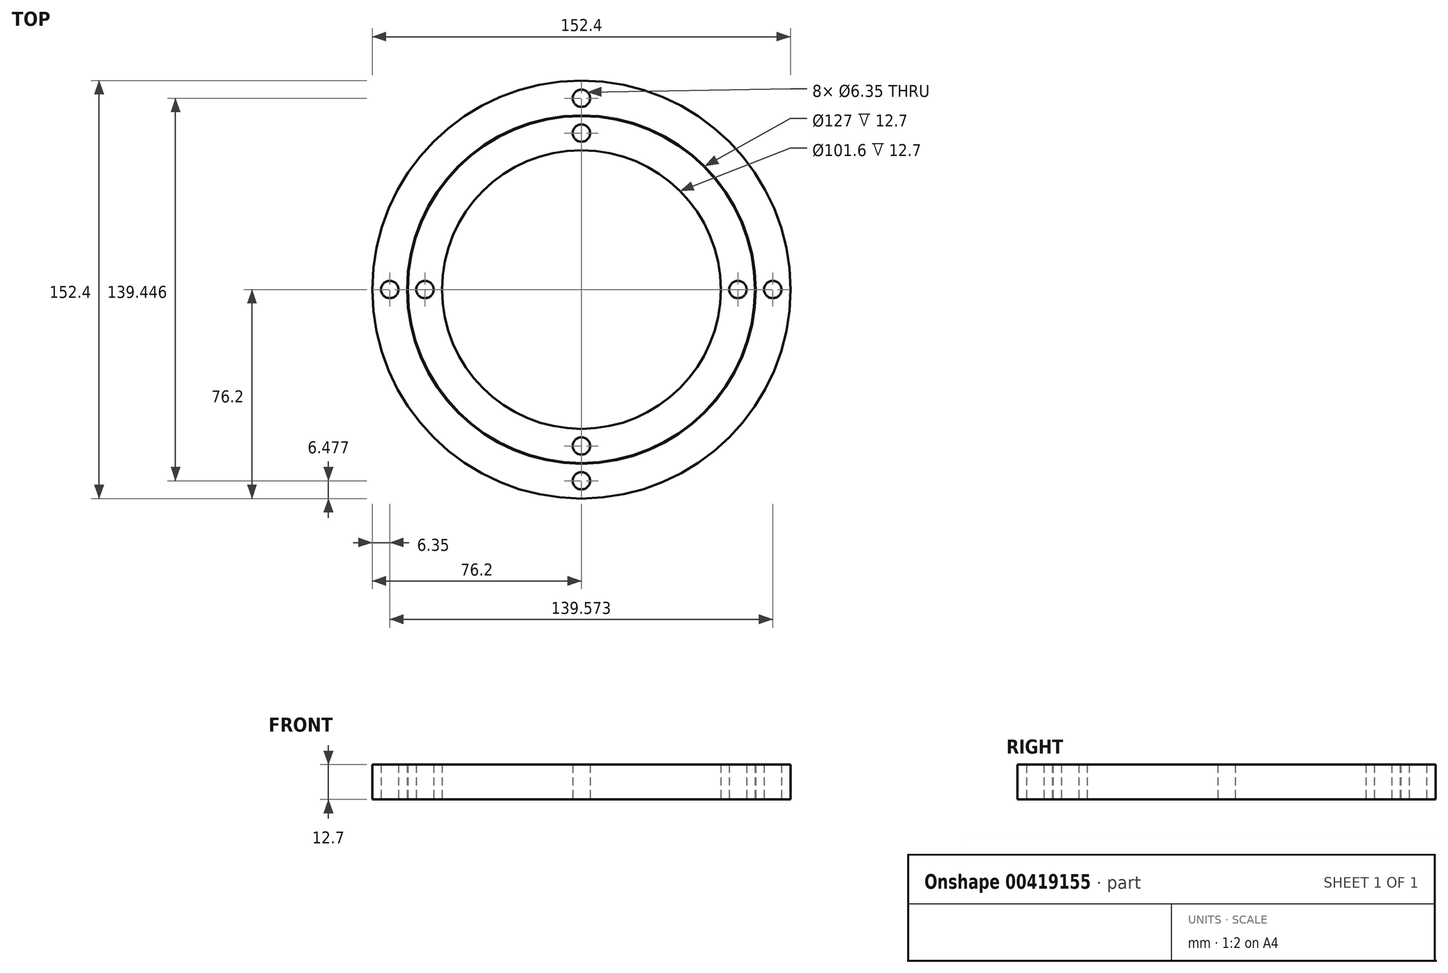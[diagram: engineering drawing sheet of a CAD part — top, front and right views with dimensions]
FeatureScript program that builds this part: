
annotation { "Feature Type Name" : "Feature", "Feature Type Description" : "" }
export const myFeature = defineFeature(function(context is Context, id is Id, definition is map)
    precondition{}
    {
        {
            var Q0;
            Q0=qCreatedBy(makeId("Top.planeOp"),FACE);
            var sketch = newSketch(context, id + "F0", { "sketchPlane" : qUnion([Q0])});
            skCircle(sketch, "E0", {"center": v(0, 0) * mm, "radius": 76.2 * mm});
            skCircle(sketch, "E1", {"center": v(0, 0) * mm, "radius": 63.5 * mm});
            skCircle(sketch, "E2", {"center": v(0, 0) * mm, "radius": 50.8 * mm});
            skCircle(sketch, "E3", {"center": v(0, 0) * mm, "radius": 63.25 * mm});
            skLineSegment(sketch, "E4", {"start": v(-76.2, 0) * mm, "end": v(-63.5, 0) * mm});
            skLineSegment(sketch, "E5", {"start": v(0, 76.2) * mm, "end": v(0, 63.25) * mm});
            skLineSegment(sketch, "E6", {"start": v(63.25, 0) * mm, "end": v(76.2, 0) * mm});
            skLineSegment(sketch, "E7", {"start": v(0, 50.8) * mm, "end": v(0, 63.25) * mm});
            skLineSegment(sketch, "E8", {"start": v(-50.8, 0) * mm, "end": v(-63.25, 0) * mm});
            skLineSegment(sketch, "E9", {"start": v(0, -50.8) * mm, "end": v(0, -63.25) * mm});
            skLineSegment(sketch, "E10", {"start": v(50.8, 0) * mm, "end": v(63.25, 0) * mm});
            skLineSegment(sketch, "E11", {"start": v(0, -63.25) * mm, "end": v(0, -76.2) * mm});
            skCircle(sketch, "E12", {"center": v(-69.85, 0) * mm, "radius": 3.18 * mm});
            skCircle(sketch, "E13", {"center": v(-57.02, 0) * mm, "radius": 3.18 * mm});
            skCircle(sketch, "E14", {"center": v(0, -69.72) * mm, "radius": 3.18 * mm});
            skCircle(sketch, "E15", {"center": v(0, 69.72) * mm, "radius": 3.18 * mm});
            skCircle(sketch, "E16", {"center": v(0, 57.02) * mm, "radius": 3.18 * mm});
            skCircle(sketch, "E17", {"center": v(69.72, 0) * mm, "radius": 3.18 * mm});
            skCircle(sketch, "E18", {"center": v(0, -57.02) * mm, "radius": 3.18 * mm});
            skCircle(sketch, "E19", {"center": v(57.02, 0) * mm, "radius": 3.18 * mm});
            skSolve(sketch);
        }
        {
            var Q0;
            {var subQ0=sQuery(id+"F0.wireOp",EDGE,"E7");var subQ5=sQuery(id+"F0.wireOp",EDGE,"E2");var subQ6=makeQuery(id+"F0.imprint","INTERSECT",VERTEX,{"derivedFrom":[subQ5,subQ0]});Q0=makeQuery(id+"F0.imprint","IMPRINT",FACE,{"disambiguationData":[TD([[makeQuery(id+"F0.imprint","IMPRINT",EDGE,{"disambiguationData":[TD([[subQ6,1.0]])],"derivedFrom":subQ5}),-1.0]])]});}
            var Q1;
            {var subQ0=sQuery(id+"F0.wireOp",EDGE,"E5");var subQ5=sQuery(id+"F0.wireOp",EDGE,"E0");var subQ6=makeQuery(id+"F0.imprint","INTERSECT",VERTEX,{"derivedFrom":[subQ5,subQ0]});Q1=makeQuery(id+"F0.imprint","IMPRINT",FACE,{"disambiguationData":[TD([[makeQuery(id+"F0.imprint","IMPRINT",EDGE,{"disambiguationData":[TD([[subQ6,1.0]])],"derivedFrom":subQ5}),1.0]])]});}
            var Q2;
            {var subQ0=sQuery(id+"F0.wireOp",EDGE,"E7");var subQ1=sQuery(id+"F0.wireOp",EDGE,"E2");var subQ2=makeQuery(id+"F0.imprint","INTERSECT",VERTEX,{"derivedFrom":[subQ1,subQ0]});Q2=makeQuery(id+"F0.imprint","IMPRINT",FACE,{"disambiguationData":[TD([[makeQuery(id+"F0.imprint","IMPRINT",EDGE,{"disambiguationData":[TD([[subQ2,-1.0]])],"derivedFrom":subQ1}),-1.0]])]});}
            var Q3;
            {var subQ0=sQuery(id+"F0.wireOp",EDGE,"E4");var subQ7=sQuery(id+"F0.wireOp",EDGE,"E0");var subQ8=makeQuery(id+"F0.imprint","INTERSECT",VERTEX,{"derivedFrom":[subQ7,subQ0]});Q3=makeQuery(id+"F0.imprint","IMPRINT",FACE,{"disambiguationData":[TD([[makeQuery(id+"F0.imprint","IMPRINT",EDGE,{"disambiguationData":[TD([[subQ8,1.0]])],"derivedFrom":subQ7}),1.0]])]});}
            var Q4;
            {var subQ0=sQuery(id+"F0.wireOp",EDGE,"E4");var subQ9=sQuery(id+"F0.wireOp",EDGE,"E0");var subQ10=makeQuery(id+"F0.imprint","INTERSECT",VERTEX,{"derivedFrom":[subQ9,subQ0]});Q4=makeQuery(id+"F0.imprint","IMPRINT",FACE,{"disambiguationData":[TD([[makeQuery(id+"F0.imprint","IMPRINT",EDGE,{"disambiguationData":[TD([[subQ10,-1.0]])],"derivedFrom":subQ9}),1.0]])]});}
            var Q5;
            {var subQ0=sQuery(id+"F0.wireOp",EDGE,"E9");var subQ1=sQuery(id+"F0.wireOp",EDGE,"E2");var subQ2=makeQuery(id+"F0.imprint","INTERSECT",VERTEX,{"derivedFrom":[subQ1,subQ0]});Q5=makeQuery(id+"F0.imprint","IMPRINT",FACE,{"disambiguationData":[TD([[makeQuery(id+"F0.imprint","IMPRINT",EDGE,{"disambiguationData":[TD([[subQ2,-1.0]])],"derivedFrom":subQ1}),-1.0]])]});}
            var Q6;
            {var subQ0=sQuery(id+"F0.wireOp",EDGE,"E6");var subQ1=sQuery(id+"F0.wireOp",EDGE,"E0");var subQ2=makeQuery(id+"F0.imprint","INTERSECT",VERTEX,{"derivedFrom":[subQ1,subQ0]});Q6=makeQuery(id+"F0.imprint","IMPRINT",FACE,{"disambiguationData":[TD([[makeQuery(id+"F0.imprint","IMPRINT",EDGE,{"disambiguationData":[TD([[subQ2,1.0]])],"derivedFrom":subQ1}),1.0]])]});}
            var Q7;
            {var subQ0=sQuery(id+"F0.wireOp",EDGE,"E8");var subQ5=sQuery(id+"F0.wireOp",EDGE,"E2");var subQ6=makeQuery(id+"F0.imprint","INTERSECT",VERTEX,{"derivedFrom":[subQ5,subQ0]});Q7=makeQuery(id+"F0.imprint","IMPRINT",FACE,{"disambiguationData":[TD([[makeQuery(id+"F0.imprint","IMPRINT",EDGE,{"disambiguationData":[TD([[subQ6,-1.0]])],"derivedFrom":subQ5}),-1.0]])]});}
            extrude(context, id + "F1", {"entities" : qUnion([Q0, Q1, Q2, Q3, Q4, Q5, Q6, Q7]), "depth" : 12.7 * mm});
        }
    });
